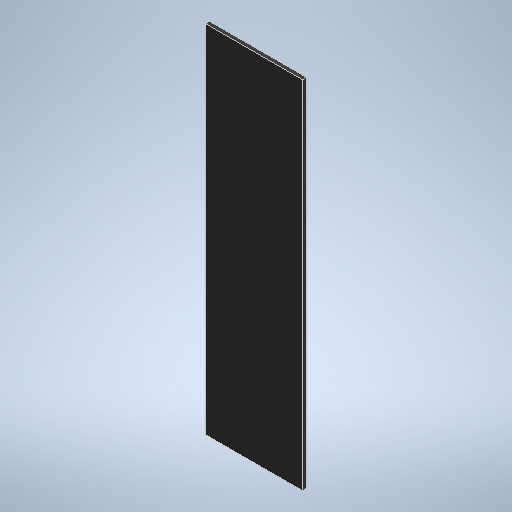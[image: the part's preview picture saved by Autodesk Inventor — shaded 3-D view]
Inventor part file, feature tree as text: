
AUTODESK INVENTOR PART (.ipt)
format: ipt  version: 2025 (Build 290162010, 162A)  size: 232,960 bytes
history: native  units: in
note: dims shown in document units (in); Inventor stores cm internally (conversion verified against a paired STEP export)
features: extrude x1, sketch x1
ambient origin geometry x8: Origin, YZ Plane, XZ Plane, XY Plane, X Axis, Y Axis, Z Axis, Center Point
bodies: Solid1 (feature_tree)
feature tree (2):
  extrude  "Extrusion1"  Depth=1.5in
  sketch  "Sketch1"  dims[d1=5.5in d2=1.5in d3=0.0625in d4=0.0in]
